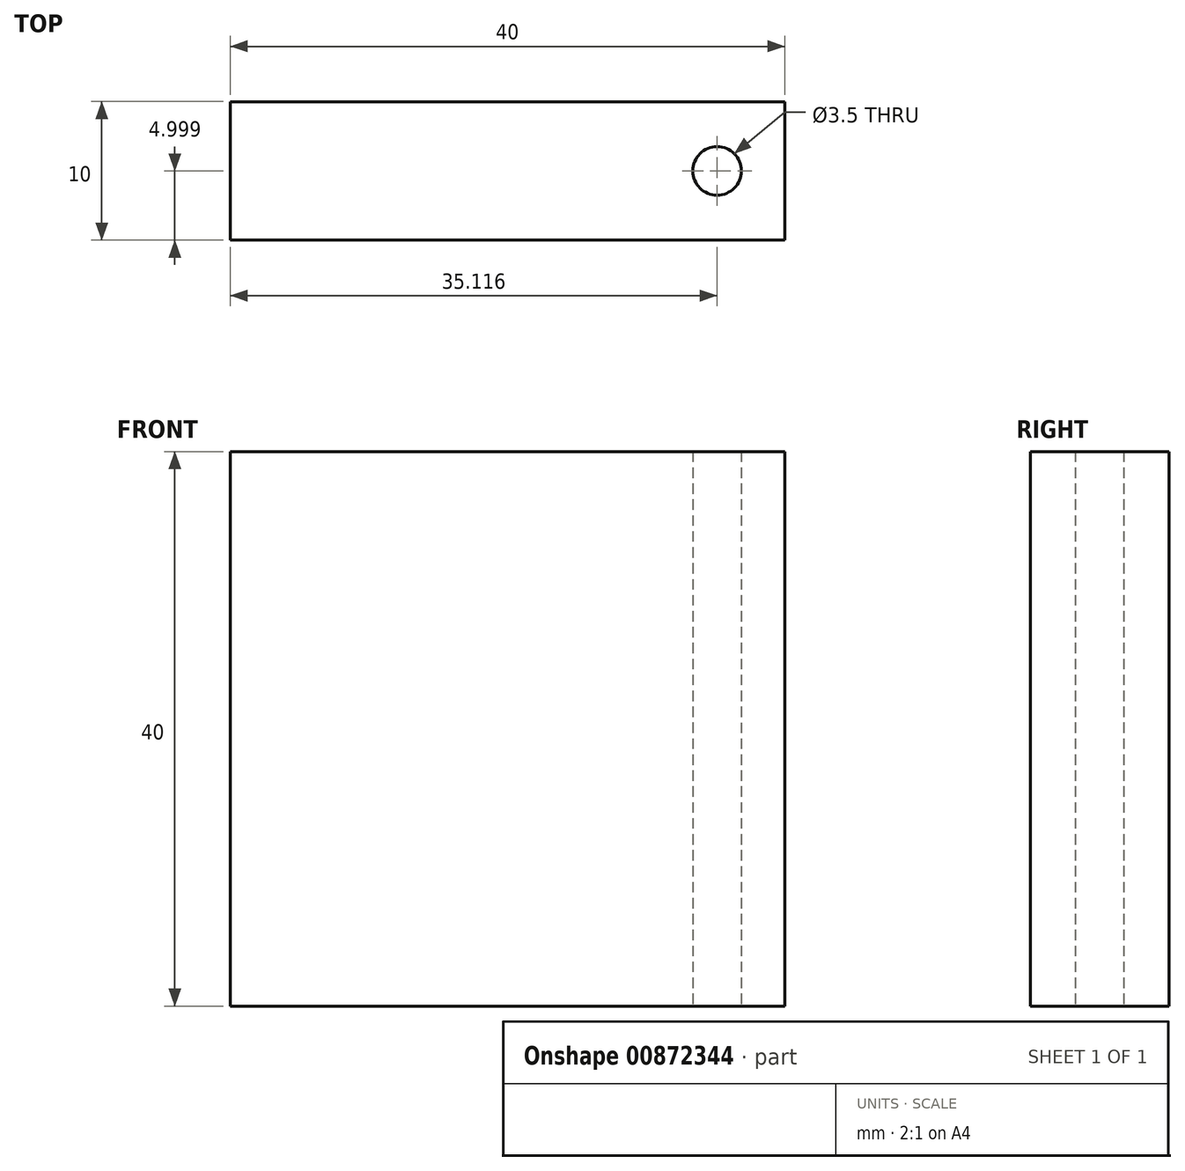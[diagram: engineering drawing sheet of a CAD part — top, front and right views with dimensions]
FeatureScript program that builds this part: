
annotation { "Feature Type Name" : "Feature", "Feature Type Description" : "" }
export const myFeature = defineFeature(function(context is Context, id is Id, definition is map)
    precondition{}
    {
        {
            var Q0;
            Q0=qCreatedBy(makeId("Top.planeOp"),FACE);
            var sketch = newSketch(context, id + "F0", { "sketchPlane" : qUnion([Q0])});
            skLineSegment(sketch, "E0", {"start": v(-16.05, 14.84) * mm, "end": v(-16.05, 4.84) * mm});
            skLineSegment(sketch, "E1", {"start": v(-16.05, 14.84) * mm, "end": v(3.95, 14.84) * mm});
            skLineSegment(sketch, "E2", {"start": v(3.95, 4.84) * mm, "end": v(-16.05, 4.84) * mm});
            skCircle(sketch, "E3", {"center": v(-11.16, 9.84) * mm, "radius": 1.75 * mm});
            skLineSegment(sketch, "E4.MirrorCS", {"start": v(23.95, 14.84) * mm, "end": v(3.95, 14.84) * mm});
            skLineSegment(sketch, "E5.MirrorCS", {"start": v(23.95, 14.84) * mm, "end": v(23.95, 4.84) * mm});
            skLineSegment(sketch, "E6.MirrorCS", {"start": v(3.95, 4.84) * mm, "end": v(23.95, 4.84) * mm});
            skCircle(sketch, "E7.MirrorC", {"center": v(19.07, 9.84) * mm, "radius": 1.75 * mm});
            skSolve(sketch);
        }
        {
            var Q0;
            Q0=makeQuery(id+"F0.imprint","IMPRINT",FACE,{"disambiguationData":[TD([[makeQuery(id+"F0.imprint","IMPRINT",EDGE,{"derivedFrom":sQuery(id+"F0.wireOp",EDGE,"E0")}),1.0]])]});
            extrude(context, id + "F1", {"entities" : qUnion([Q0]), "depth" : 3 * mm, "offsetDistance" : 25 * mm});
        }
        {
            var Q0;
            Q0=makeQuery(id+"F0.imprint","IMPRINT",FACE,{"disambiguationData":[TD([[makeQuery(id+"F0.imprint","IMPRINT",EDGE,{"derivedFrom":sQuery(id+"F0.wireOp",EDGE,"E7.MirrorC")}),-1.0]])]});
            var Q1;
            Q1=makeQuery(id+"F0.imprint","IMPRINT",FACE,{"disambiguationData":[TD([[makeQuery(id+"F0.imprint","IMPRINT",EDGE,{"derivedFrom":sQuery(id+"F0.wireOp",EDGE,"E3")}),1.0]])]});
            extrude(context, id + "F2", {"entities" : qUnion([Q0, Q1]), "operationType" : NewBodyOperationType.ADD, "depth" : 40 * mm, "offsetDistance" : 25 * mm});
        }
    });
